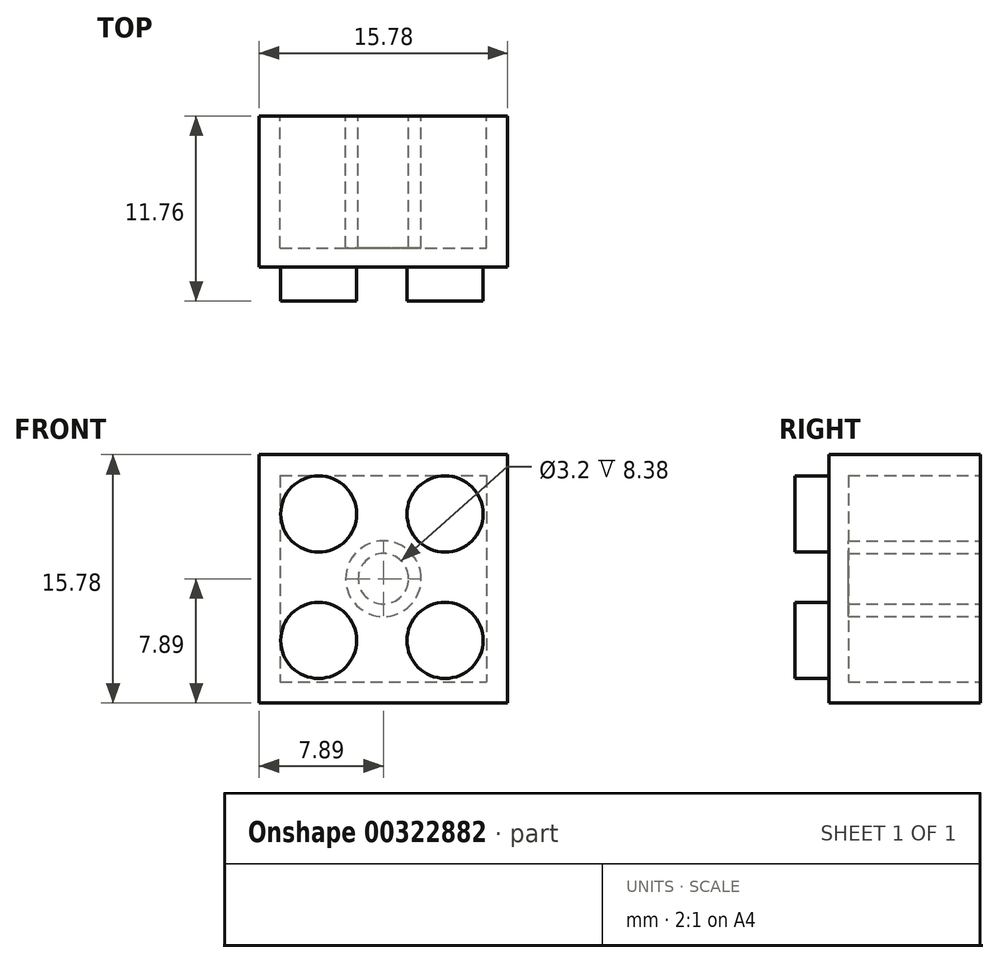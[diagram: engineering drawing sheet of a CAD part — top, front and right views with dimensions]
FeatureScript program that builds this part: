
annotation { "Feature Type Name" : "Feature", "Feature Type Description" : "" }
export const myFeature = defineFeature(function(context is Context, id is Id, definition is map)
    precondition{}
    {
        {
            var Q0;
            Q0=qCreatedBy(makeId("Front.planeOp"),FACE);
            var sketch = newSketch(context, id + "F0", { "sketchPlane" : qUnion([Q0])});
            skLineSegment(sketch, "E0.bottom", {"start": v(7.89, 7.9) * mm, "end": v(-7.9, 7.89) * mm});
            skLineSegment(sketch, "E0.top", {"start": v(7.89, -7.89) * mm, "end": v(-7.89, -7.9) * mm});
            skLineSegment(sketch, "E0.left", {"start": v(7.89, 7.9) * mm, "end": v(7.89, -7.89) * mm});
            skLineSegment(sketch, "E0.right", {"start": v(-7.9, 7.89) * mm, "end": v(-7.89, -7.9) * mm});
            skPoint(sketch, "E0.middle", {"position": v(0, 0) * mm});
            skCircle(sketch, "E1", {"center": v(-4.11, 4.11) * mm, "radius": 2.42 * mm});
            skCircle(sketch, "E2", {"center": v(3.92, 4.11) * mm, "radius": 2.42 * mm});
            skCircle(sketch, "E3", {"center": v(-4.11, -3.92) * mm, "radius": 2.42 * mm});
            skCircle(sketch, "E4", {"center": v(3.92, -3.92) * mm, "radius": 2.42 * mm});
            skSolve(sketch);
        }
        {
            var Q0;
            Q0=makeQuery(id+"F0.imprint","IMPRINT",FACE,{"disambiguationData":[TD([[makeQuery(id+"F0.imprint","IMPRINT",EDGE,{"derivedFrom":sQuery(id+"F0.wireOp",EDGE,"E0.bottom")}),1.0]])]});
            extrude(context, id + "F1", {"entities" : qUnion([Q0]), "offsetDistance" : 25 * mm, "depth" : 9.6 * mm});
        }
        {
            var Q0;
            Q0=makeQuery(id+"F0.imprint","IMPRINT",FACE,{"disambiguationData":[TD([[makeQuery(id+"F0.imprint","IMPRINT",EDGE,{"derivedFrom":sQuery(id+"F0.wireOp",EDGE,"E1")}),1.0]])]});
            var Q1;
            Q1=makeQuery(id+"F0.imprint","IMPRINT",FACE,{"disambiguationData":[TD([[makeQuery(id+"F0.imprint","IMPRINT",EDGE,{"derivedFrom":sQuery(id+"F0.wireOp",EDGE,"E2")}),1.0]])]});
            var Q2;
            Q2=makeQuery(id+"F0.imprint","IMPRINT",FACE,{"disambiguationData":[TD([[makeQuery(id+"F0.imprint","IMPRINT",EDGE,{"derivedFrom":sQuery(id+"F0.wireOp",EDGE,"E3")}),1.0]])]});
            var Q3;
            Q3=makeQuery(id+"F0.imprint","IMPRINT",FACE,{"disambiguationData":[TD([[makeQuery(id+"F0.imprint","IMPRINT",EDGE,{"derivedFrom":sQuery(id+"F0.wireOp",EDGE,"E4")}),1.0]])]});
            extrude(context, id + "F2", {"entities" : qUnion([Q0, Q1, Q2, Q3]), "operationType" : NewBodyOperationType.ADD, "offsetDistance" : 25 * mm, "depth" : 11.76 * mm});
        }
        {
            var Q0;
            Q0=makeQuery(id+"F0.imprint","IMPRINT",FACE,{"disambiguationData":[TD([[makeQuery(id+"F0.imprint","IMPRINT",EDGE,{"derivedFrom":sQuery(id+"F0.wireOp",EDGE,"E0.bottom")}),1.0]])]});
            var sketch = newSketch(context, id + "F3", { "sketchPlane" : qUnion([Q0])});
            skLineSegment(sketch, "E5.bottom", {"start": v(-6.56, 6.56) * mm, "end": v(6.56, 6.56) * mm});
            skLineSegment(sketch, "E5.top", {"start": v(-6.56, -6.56) * mm, "end": v(6.56, -6.56) * mm});
            skLineSegment(sketch, "E5.left", {"start": v(-6.56, 6.56) * mm, "end": v(-6.56, -6.56) * mm});
            skLineSegment(sketch, "E5.right", {"start": v(6.56, 6.56) * mm, "end": v(6.56, -6.56) * mm});
            skPoint(sketch, "E5.middle", {"position": v(0, 0) * mm});
            skCircle(sketch, "E6", {"center": v(0, 0) * mm, "radius": 2.4 * mm});
            skCircle(sketch, "E7", {"center": v(0, 0) * mm, "radius": 1.6 * mm});
            skSolve(sketch);
        }
        {
            var Q0;
            Q0=makeQuery(id+"F3.imprint","IMPRINT",FACE,{"disambiguationData":[TD([[makeQuery(id+"F3.imprint","IMPRINT",EDGE,{"derivedFrom":sQuery(id+"F3.wireOp",EDGE,"E5.bottom")}),-1.0]])]});
            extrude(context, id + "F4", {"entities" : qUnion([Q0]), "operationType" : NewBodyOperationType.REMOVE, "offsetDistance" : 25 * mm, "depth" : 8.38 * mm});
        }
        {
            var Q0;
            Q0=makeQuery(id+"F0.imprint","IMPRINT",FACE,{"disambiguationData":[TD([[makeQuery(id+"F0.imprint","IMPRINT",EDGE,{"derivedFrom":sQuery(id+"F0.wireOp",EDGE,"E2")}),1.0]])]});
            var Q1;
            Q1=makeQuery(id+"F0.imprint","IMPRINT",FACE,{"disambiguationData":[TD([[makeQuery(id+"F0.imprint","IMPRINT",EDGE,{"derivedFrom":sQuery(id+"F0.wireOp",EDGE,"E1")}),1.0]])]});
            var Q2;
            Q2=makeQuery(id+"F0.imprint","IMPRINT",FACE,{"disambiguationData":[TD([[makeQuery(id+"F0.imprint","IMPRINT",EDGE,{"derivedFrom":sQuery(id+"F0.wireOp",EDGE,"E4")}),1.0]])]});
            var Q3;
            Q3=makeQuery(id+"F0.imprint","IMPRINT",FACE,{"disambiguationData":[TD([[makeQuery(id+"F0.imprint","IMPRINT",EDGE,{"derivedFrom":sQuery(id+"F0.wireOp",EDGE,"E3")}),1.0]])]});
            var Q4;
            Q4=makeQuery(id+"F3.imprint","IMPRINT",FACE,{"disambiguationData":[TD([[makeQuery(id+"F3.imprint","IMPRINT",EDGE,{"derivedFrom":sQuery(id+"F3.wireOp",EDGE,"E7")}),1.0]])]});
            extrude(context, id + "F5", {"entities" : qUnion([Q0, Q1, Q2, Q3, Q4]), "operationType" : NewBodyOperationType.REMOVE, "depth" : 8.38 * mm});
        }
    });
